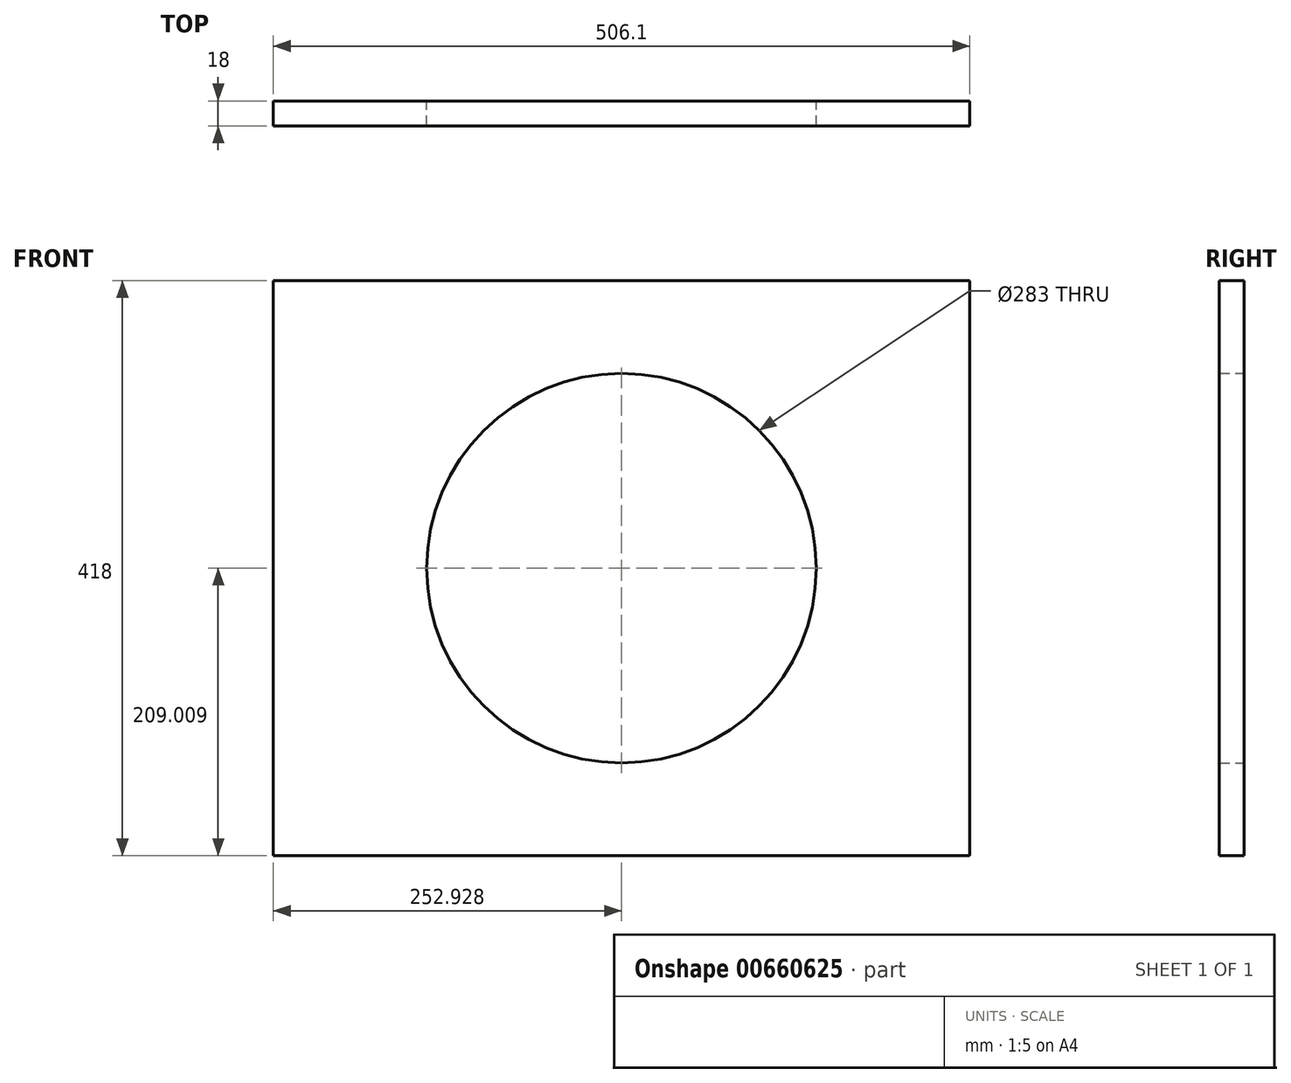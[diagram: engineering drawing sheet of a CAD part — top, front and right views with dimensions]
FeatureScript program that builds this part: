
annotation { "Feature Type Name" : "Feature", "Feature Type Description" : "" }
export const myFeature = defineFeature(function(context is Context, id is Id, definition is map)
    precondition{}
    {
        {
            var Q0;
            Q0=qCreatedBy(makeId("Front.planeOp"),FACE);
            var sketch = newSketch(context, id + "F0", { "sketchPlane" : qUnion([Q0])});
            skLineSegment(sketch, "E0.bottom", {"start": v(-245.3, 260.55) * mm, "end": v(260.8, 260.55) * mm});
            skLineSegment(sketch, "E0.top", {"start": v(-245.3, -157.45) * mm, "end": v(260.8, -157.45) * mm});
            skLineSegment(sketch, "E0.left", {"start": v(-245.3, 260.55) * mm, "end": v(-245.3, -157.45) * mm});
            skLineSegment(sketch, "E0.right", {"start": v(260.8, 260.55) * mm, "end": v(260.8, -157.45) * mm});
            skSolve(sketch);
        }
        {
            var Q0;
            Q0=qCreatedBy(makeId("Front.planeOp"),FACE);
            var sketch = newSketch(context, id + "F1", { "sketchPlane" : qUnion([Q0])});
            skCircle(sketch, "E1", {"center": v(7.62, 51.56) * mm, "radius": 141.5 * mm});
            skSolve(sketch);
        }
        {
            var Q0;
            Q0 = qSketchRegion(id + "F0", true);
            extrude(context, id + "F2", {"entities" : qUnion([Q0]), "depth" : 18 * mm, "offsetDistance" : 25 * mm});
        }
        {
            var Q0;
            Q0 = qSketchRegion(id + "F1", true);
            extrude(context, id + "F3", {"entities" : qUnion([Q0]), "operationType" : NewBodyOperationType.REMOVE, "endBound" : BoundingType.THROUGH_ALL, "depth" : 25 * mm, "offsetDistance" : 25 * mm});
        }
    });
